# Revit family: Chair-Multi_Purpose-Allermuir-Mollie-A583
name_source: partatom
category: Furniture
revit_build: Autodesk Revit Architecture 2012 (Build: 20110309_2315(x64)
units: mm (PartAtom-declared; Revit-internal decimal feet)

## types (1)
- A583
    04 CSI = 12 51 00
    95 CSI = 12510
    Arms Height = 37"
    Assembly Code = E2020200
    Base = Metal - Allermuir - Chrome - Polished
    Brochure URL = http://www.allermuir.net
    CAD Blocks URL = http://www.allermuir.net
    Color Availability = See price list for material options
    Description = High stool 4 leg
    Fabric Spec Sheets = http://www.allermuir.net
    Manufacturer = Allermuir
    Manufacturer Fax = (419) 887 5805
    Model = A583
    Optional Feature Notes = Beech clear finish shell
    Overall Depth = 20"
    Overall Height = 39 51/128"
    Overall Width = 22"
    Plastic Arms in Black = No
    Plastic glides = Yes
    Plugin Data URL = http://products.ecoscorecard.com
    Pricing URL = http://www.allermuir.net
    Product Line = Mollie
    Product Page URL = http://www.allermuir.net
    Seat Depth = 17 77/256"
    Seat Height = 28 61/64"
    Seat Padding = Plastic  - Allermuir - Black - Smooth
    Seat Width = 18"
    Seat or Top = Fabric - Allermuir - Upholstery - Pebbled - Light Brown
    Specifications URL = http://www.allermuir.net
    Stacks = No
    Subcategory = Multi-Purpose Line
    Tubular Steel Legs = Yes
    URL = http://www.allermuir.net
    Upholstered Back = Yes
    Upholstered Seat = Yes
    Weight = 35.0 lb
    ecoScorecard Product Page = http://products.ecoscorecard.com
    ecoScorecard_data = http://thesenatorgroup.ecoscorecard.com

## geometry (parser evidence)
native form markers: Blend x5, Sweep x5
no freeform markers — native parametric forms only
